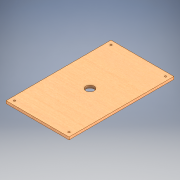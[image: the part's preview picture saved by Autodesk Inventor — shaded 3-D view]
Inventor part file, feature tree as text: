
AUTODESK INVENTOR PART (.ipt)
format: ipt  version: 2020 (Build 240168000, 168)  size: 123,904 bytes
history: native  units: mm
features: extrude x1, sketch x1
ambient origin geometry x8: Origin, YZ Plane, XZ Plane, XY Plane, X Axis, Y Axis, Z Axis, Center Point
bodies: Solide1 (feature_tree)
feature tree (2):
  extrude  "Extrusion1"  Depth=150.0mm
  sketch  "Esquisse1"
